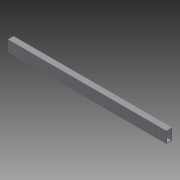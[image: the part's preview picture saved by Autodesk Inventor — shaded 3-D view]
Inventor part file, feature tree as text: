
AUTODESK INVENTOR PART (.ipt)
format: ipt  version: 2015 SP1 (Build 190203100, 203)  size: 102,912 bytes
history: native  units: in
note: dims shown in document units (in); Inventor stores cm internally (conversion verified against a paired STEP export)
features: sketch x3, hole x2, projected_geometry x2, extrude x1
ambient origin geometry x8: Origin, YZ Plane, XZ Plane, XY Plane, X Axis, Y Axis, Z Axis, Center Point
bodies: Solid1 (feature_tree)
feature tree (8):
  extrude  "Extrusion1"  Depth=1.0in
  hole  "Hole3"  [1 undecoded]
  hole  "Hole4"  [1 undecoded]
  sketch  "Sketch1"  dims[d0=2.0in d1=1.0in]
  sketch  "Sketch2"  dims[d2=1.75in d3=0.75in]
  projected_geometry  "Projected Loop1"
  sketch  "Sketch3"  dims[d4=0.125in d5=0.125in d6=28.0in d7=0.0in d8=1.25in d9=1.0in d10=1.25in d11=1.0in d30=0.25in d31=0.75in d32=0.375in d33=0.25in d34=0.5635in d35=1.0in d36=0.8108in d37=3.75in d38=1.0in d39=1.0in d40=3.75in d41=0.25in d42=0.75in d43=0.375in d44=0.25in d45=0.5635in d46=1.0in d47=0.8108in]
  projected_geometry  "Projected Loop2"
note: 2 required parameter values undecoded (feature->parameter linkage not recoverable at this tier; creation-order binding heuristic only, values carry confidence <= 0.55)
